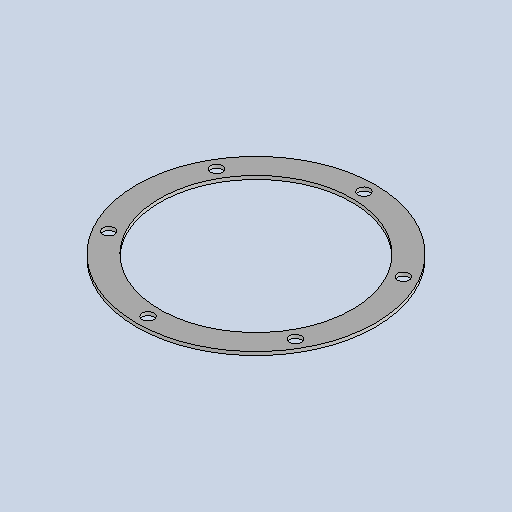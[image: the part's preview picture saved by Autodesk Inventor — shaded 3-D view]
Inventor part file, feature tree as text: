
AUTODESK INVENTOR PART (.ipt)
format: ipt  version: 2025 (Build 290162010, 162A)  size: 215,040 bytes
history: native  units: mm
features: sketch x2, other x2, sheet_metal_op x1, extrude x1, pattern_circular x1, projected_geometry x1
ambient origin geometry x8: Origin, YZ Plane, XZ Plane, XY Plane, X Axis, Y Axis, Z Axis, Center Point
bodies: Solid1 (feature_tree)
feature tree (8):
  sheet_metal_op  "Face1"
  extrude  "Extrusion1"  TaperAngle=0.0deg  [1 undecoded]
  pattern_circular  "Circular Pattern2"  Count=6 Angle=360.0deg
  sketch  "Sketch1"  dims[d2=3.0mm d4=0.0mm d5=0.0mm]
  other  "Plate1"
  sketch  "Sketch2"  dims[d21=10.0mm d27=60.0mm d28=360.0deg d30=165.0mm d31=185.0mm d32=205.0mm]
  projected_geometry  "Projected Loop1"
  other  "Definition1"
note: 1 required parameter value undecoded (feature->parameter linkage not recoverable at this tier; creation-order binding heuristic only, values carry confidence <= 0.55)
